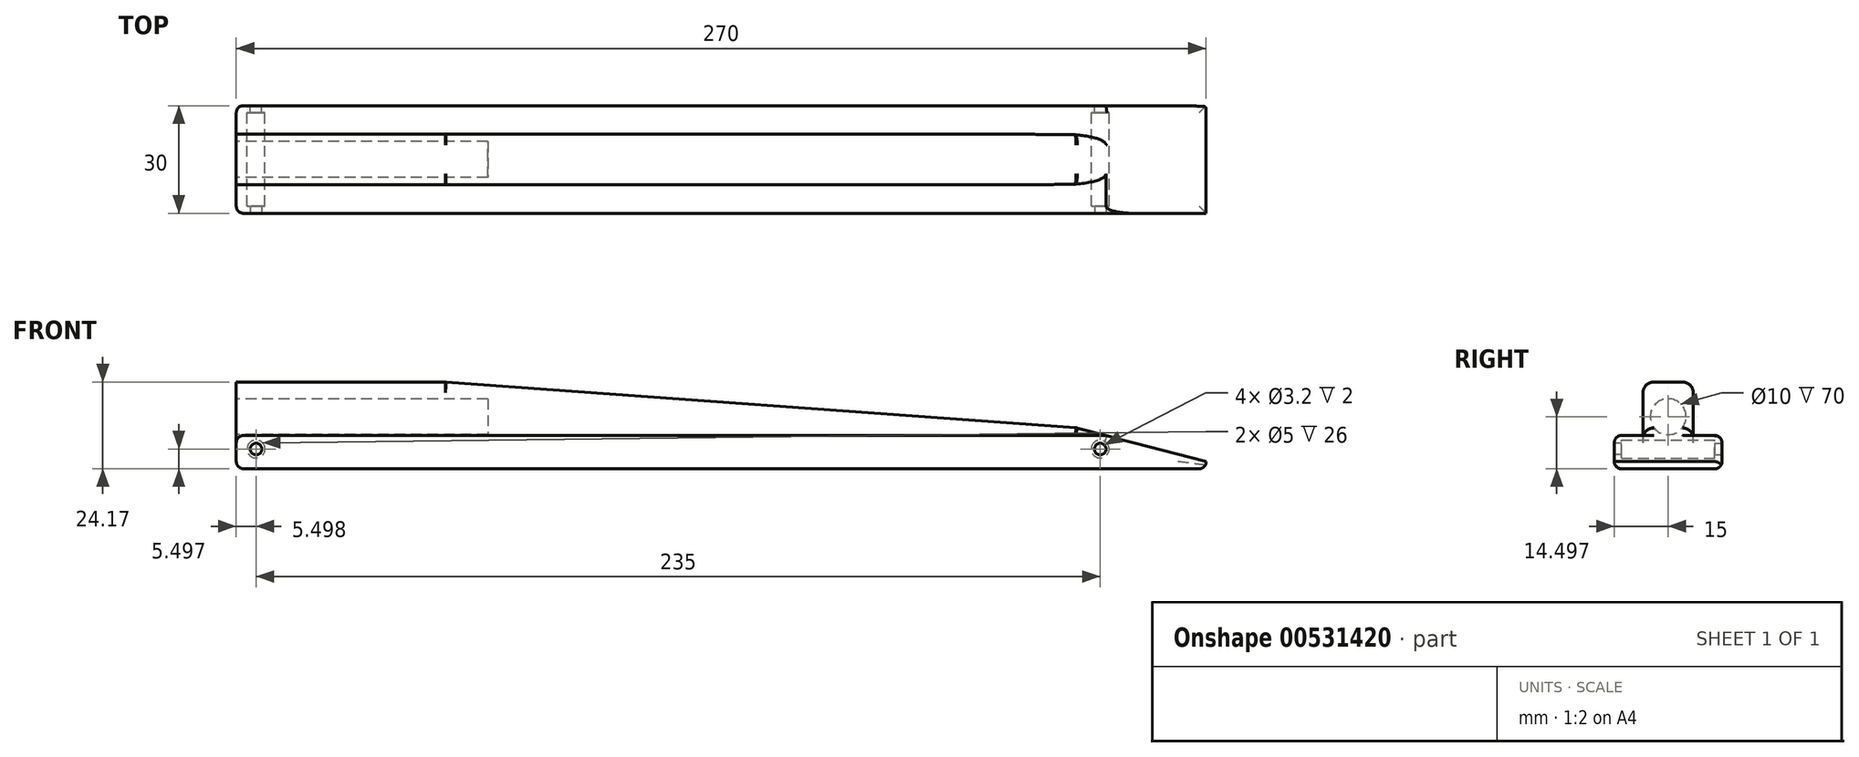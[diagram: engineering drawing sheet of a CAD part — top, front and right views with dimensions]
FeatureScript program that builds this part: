
annotation { "Feature Type Name" : "Feature", "Feature Type Description" : "" }
export const myFeature = defineFeature(function(context is Context, id is Id, definition is map)
    precondition{}
    {
        {
            var Q0;
            Q0=qCreatedBy(makeId("Front.planeOp"),FACE);
            var sketch = newSketch(context, id + "F0", { "sketchPlane" : qUnion([Q0])});
            skLineSegment(sketch, "E0.bottom", {"start": v(-113.44, 3.04) * mm, "end": v(136.56, 3.04) * mm});
            skLineSegment(sketch, "E0.top", {"start": v(-113.44, -36.96) * mm, "end": v(136.56, -36.96) * mm});
            skLineSegment(sketch, "E0.left", {"start": v(-113.44, 3.04) * mm, "end": v(-113.44, -36.96) * mm});
            skLineSegment(sketch, "E0.right", {"start": v(136.56, 3.04) * mm, "end": v(136.56, -36.96) * mm});
            skCircle(sketch, "E1", {"center": v(-107.94, -31.46) * mm, "radius": 2.5 * mm});
            skCircle(sketch, "E2", {"center": v(-107.94, -31.46) * mm, "radius": 1.6 * mm});
            skCircle(sketch, "E3", {"center": v(127.06, -31.46) * mm, "radius": 2.5 * mm});
            skCircle(sketch, "E4", {"center": v(127.06, -31.46) * mm, "radius": 1.6 * mm});
            skSolve(sketch);
        }
        {
            var Q0;
            Q0=makeQuery(id+"F0.imprint","IMPRINT",FACE,{"disambiguationData":[TD([[makeQuery(id+"F0.imprint","IMPRINT",EDGE,{"derivedFrom":sQuery(id+"F0.wireOp",EDGE,"E0.bottom")}),-1.0]])]});
            extrude(context, id + "F1", {"entities" : qUnion([Q0]), "depth" : 15 * mm, "offsetDistance" : 25 * mm, "hasSecondDirection" : true, "secondDirectionOppositeDirection" : true, "secondDirectionDepth" : 15 * mm});
        }
        {
            var Q0;
            Q0=makeQuery(id+"F1.opExtrude","CAP_FACE",FACE,{"disambiguationData":[OSD([sQuery(id+"F0.wireOp",EDGE,"E0.bottom"),sQuery(id+"F0.wireOp",EDGE,"E0.top"),sQuery(id+"F0.wireOp",EDGE,"E0.left"),sQuery(id+"F0.wireOp",EDGE,"E0.right"),sQuery(id+"F0.wireOp",EDGE,"E1"),sQuery(id+"F0.wireOp",EDGE,"E3")])],"isStart":false});
            var sketch = newSketch(context, id + "F2", { "sketchPlane" : qUnion([Q0])});
            skLineSegment(sketch, "E5.bottom", {"start": v(-113.44, 3.04) * mm, "end": v(136.56, 3.04) * mm});
            skLineSegment(sketch, "E5.top", {"start": v(-113.44, -36.96) * mm, "end": v(136.56, -36.96) * mm});
            skLineSegment(sketch, "E5.left", {"start": v(-113.44, 3.04) * mm, "end": v(-113.44, -36.96) * mm});
            skLineSegment(sketch, "E5.right", {"start": v(136.56, 3.04) * mm, "end": v(136.56, -36.96) * mm});
            skCircle(sketch, "E6", {"center": v(-107.94, -31.46) * mm, "radius": 2.5 * mm});
            skCircle(sketch, "E7", {"center": v(-107.94, -31.46) * mm, "radius": 1.6 * mm});
            skCircle(sketch, "E8", {"center": v(127.06, -31.46) * mm, "radius": 2.5 * mm});
            skCircle(sketch, "E9", {"center": v(127.06, -31.46) * mm, "radius": 1.6 * mm});
            skSolve(sketch);
        }
        {
            var Q0;
            Q0=makeQuery(id+"F2.imprint","IMPRINT",FACE,{"disambiguationData":[TD([[makeQuery(id+"F2.imprint","IMPRINT",EDGE,{"derivedFrom":sQuery(id+"F2.wireOp",EDGE,"E6")}),1.0]])]});
            var Q1;
            Q1=makeQuery(id+"F2.imprint","IMPRINT",FACE,{"disambiguationData":[TD([[makeQuery(id+"F2.imprint","IMPRINT",EDGE,{"derivedFrom":sQuery(id+"F2.wireOp",EDGE,"E8")}),1.0]])]});
            extrude(context, id + "F3", {"entities" : qUnion([Q0, Q1]), "operationType" : NewBodyOperationType.ADD, "oppositeDirection" : true, "depth" : 2 * mm, "offsetDistance" : 25 * mm});
        }
        {
            var Q0;
            Q0=makeQuery(id+"F1.opExtrude","CAP_FACE",FACE,{"disambiguationData":[OSD([sQuery(id+"F0.wireOp",EDGE,"E0.bottom"),sQuery(id+"F0.wireOp",EDGE,"E0.top"),sQuery(id+"F0.wireOp",EDGE,"E0.left"),sQuery(id+"F0.wireOp",EDGE,"E0.right"),sQuery(id+"F0.wireOp",EDGE,"E1"),sQuery(id+"F0.wireOp",EDGE,"E3")])],"isStart":true});
            var sketch = newSketch(context, id + "F4", { "sketchPlane" : qUnion([Q0])});
            skLineSegment(sketch, "E10.bottom", {"start": v(-136.56, 3.04) * mm, "end": v(113.44, 3.04) * mm});
            skLineSegment(sketch, "E10.top", {"start": v(-136.56, -36.96) * mm, "end": v(113.44, -36.96) * mm});
            skLineSegment(sketch, "E10.left", {"start": v(-136.56, 3.04) * mm, "end": v(-136.56, -36.96) * mm});
            skLineSegment(sketch, "E10.right", {"start": v(113.44, 3.04) * mm, "end": v(113.44, -36.96) * mm});
            skCircle(sketch, "E11", {"center": v(-127.06, -31.46) * mm, "radius": 2.5 * mm});
            skCircle(sketch, "E12", {"center": v(-127.06, -31.46) * mm, "radius": 1.6 * mm});
            skCircle(sketch, "E13", {"center": v(107.94, -31.46) * mm, "radius": 2.5 * mm});
            skCircle(sketch, "E14", {"center": v(107.94, -31.46) * mm, "radius": 1.6 * mm});
            skSolve(sketch);
        }
        {
            var Q0;
            Q0=makeQuery(id+"F4.imprint","IMPRINT",FACE,{"disambiguationData":[TD([[makeQuery(id+"F4.imprint","IMPRINT",EDGE,{"derivedFrom":sQuery(id+"F4.wireOp",EDGE,"E13")}),-1.0]])]});
            var Q1;
            Q1=makeQuery(id+"F4.imprint","IMPRINT",FACE,{"disambiguationData":[TD([[makeQuery(id+"F4.imprint","IMPRINT",EDGE,{"derivedFrom":sQuery(id+"F4.wireOp",EDGE,"E11")}),-1.0]])]});
            extrude(context, id + "F5", {"entities" : qUnion([Q0, Q1]), "operationType" : NewBodyOperationType.ADD, "oppositeDirection" : true, "depth" : 2 * mm, "offsetDistance" : 25 * mm});
        }
        {
            var Q0;
            Q0=makeQuery(id+"F1.opExtrude","SWEPT_FACE",FACE,{"disambiguationData":[OSD([sQuery(id+"F0.wireOp",EDGE,"E0.left")])]});
            var sketch = newSketch(context, id + "F6", { "sketchPlane" : qUnion([Q0])});
            skCircle(sketch, "E15", {"center": v(0, -22.46) * mm, "radius": 5 * mm});
            skPoint(sketch, "E15.centerSnap0", {"position": v(0, -36.96) * mm});
            skSolve(sketch);
        }
        {
            var Q0;
            Q0=makeQuery(id+"F6.imprint","IMPRINT",FACE,{"disambiguationData":[TD([[makeQuery(id+"F6.imprint","IMPRINT",EDGE,{"derivedFrom":sQuery(id+"F6.wireOp",EDGE,"E15")}),1.0]])]});
            extrude(context, id + "F7", {"entities" : qUnion([Q0]), "operationType" : NewBodyOperationType.REMOVE, "oppositeDirection" : true, "depth" : 70 * mm, "offsetDistance" : 25 * mm});
        }
        {
            var Q0;
            Q0=makeQuery(id+"F1.opExtrude","SWEPT_FACE",FACE,{"disambiguationData":[OSD([sQuery(id+"F0.wireOp",EDGE,"E0.right")])]});
            extrude(context, id + "F8", {"entities" : qUnion([Q0]), "operationType" : NewBodyOperationType.ADD, "depth" : 20 * mm, "offsetDistance" : 25 * mm});
        }
        {
            var Q0;
            {var subQ0=sQuery(id+"F0.wireOp",EDGE,"E0.right");Q0=makeQuery(id+"F8.boolean.opBoolean","MERGE",FACE,{"derivedFrom":[makeQuery(id+"F3.boolean.opBoolean","MERGE",FACE,{"derivedFrom":[makeQuery(id+"F1.opExtrude","CAP_FACE",FACE,{"disambiguationData":[OSD([sQuery(id+"F0.wireOp",EDGE,"E0.bottom"),sQuery(id+"F0.wireOp",EDGE,"E0.top"),sQuery(id+"F0.wireOp",EDGE,"E0.left"),subQ0,sQuery(id+"F0.wireOp",EDGE,"E1"),sQuery(id+"F0.wireOp",EDGE,"E3")])],"isStart":false}),makeQuery(id+"F3.opExtrude","CAP_FACE",FACE,{"disambiguationData":[OSD([sQuery(id+"F2.wireOp",EDGE,"E6"),sQuery(id+"F2.wireOp",EDGE,"E7")])],"isStart":true}),makeQuery(id+"F3.opExtrude","CAP_FACE",FACE,{"disambiguationData":[OSD([sQuery(id+"F2.wireOp",EDGE,"E8"),sQuery(id+"F2.wireOp",EDGE,"E9")])],"isStart":true})]}),makeQuery(id+"F8.opExtrude","SWEPT_FACE",FACE,{"disambiguationData":[OSD([subQ0]),TDD([makeQuery(id+"F1.opExtrude","CAP_EDGE",EDGE,{"disambiguationData":[OSD([subQ0])],"isStart":false})])]})]});}
            var sketch = newSketch(context, id + "F9", { "sketchPlane" : qUnion([Q0])});
            skLineSegment(sketch, "E16", {"start": v(156.56, -34.96) * mm, "end": v(120.52, -25.57) * mm});
            skLineSegment(sketch, "E17", {"start": v(120.52, -25.57) * mm, "end": v(-55.11, -12.8) * mm});
            skLineSegment(sketch, "E18", {"start": v(-55.11, -12.8) * mm, "end": v(-113.44, -12.8) * mm});
            skSolve(sketch);
        }
        {
            var Q0;
            {var subQ4=sQuery(id+"F9.wireOp",EDGE,"E16");Q0=makeQuery(id+"F9.imprint","IMPRINT",FACE,{"disambiguationData":[TD([[makeQuery(id+"F9.imprint","IMPRINT",EDGE,{"derivedFrom":subQ4}),-1.0]])]});}
            extrude(context, id + "F10", {"entities" : qUnion([Q0]), "operationType" : NewBodyOperationType.REMOVE, "endBound" : BoundingType.THROUGH_ALL, "oppositeDirection" : true, "depth" : 25 * mm, "offsetDistance" : 25 * mm});
        }
        {
            var Q0;
            Q0=makeQuery(id+"F10.boolean.opBoolean","COPY",EDGE,{"derivedFrom":makeQuery(id+"F10.opExtrude","SWEPT_EDGE",EDGE,{"disambiguationData":[OSD([sQuery(id+"F0.wireOp",EDGE,"E0.right"),sQuery(id+"F9.wireOp",EDGE,"E16")])]})});
            var Q1;
            Q1=makeQuery(id+"F10.boolean.opBoolean","COPY",EDGE,{"derivedFrom":makeQuery(id+"F10.opExtrude","SWEPT_EDGE",EDGE,{"disambiguationData":[OSD([sQuery(id+"F9.wireOp",EDGE,"E16"),sQuery(id+"F9.wireOp",EDGE,"E17")])]})});
            var Q2;
            Q2=makeQuery(id+"F10.boolean.opBoolean","COPY",EDGE,{"derivedFrom":makeQuery(id+"F10.opExtrude","CAP_EDGE",EDGE,{"disambiguationData":[OSD([sQuery(id+"F9.wireOp",EDGE,"E18")])],"isStart":true})});
            var Q3;
            Q3=makeQuery(id+"F10.boolean.opBoolean","COPY",EDGE,{"derivedFrom":makeQuery(id+"F10.opExtrude","CAP_EDGE",EDGE,{"disambiguationData":[OSD([sQuery(id+"F9.wireOp",EDGE,"E17")])],"isStart":true})});
            var Q4;
            Q4=makeQuery(id+"F10.boolean.opBoolean","COPY",EDGE,{"derivedFrom":makeQuery(id+"F10.opExtrude","CAP_EDGE",EDGE,{"disambiguationData":[OSD([sQuery(id+"F9.wireOp",EDGE,"E16")])],"isStart":true})});
            var Q5;
            {var subQ0=sQuery(id+"F0.wireOp",EDGE,"E0.right");Q5=makeQuery(id+"F10.boolean.opBoolean","INTERSECT",EDGE,{"derivedFrom":[makeQuery(id+"F8.boolean.opBoolean","MERGE",FACE,{"derivedFrom":[makeQuery(id+"F5.boolean.opBoolean","MERGE",FACE,{"derivedFrom":[makeQuery(id+"F1.opExtrude","CAP_FACE",FACE,{"disambiguationData":[OSD([sQuery(id+"F0.wireOp",EDGE,"E0.bottom"),sQuery(id+"F0.wireOp",EDGE,"E0.top"),sQuery(id+"F0.wireOp",EDGE,"E0.left"),subQ0,sQuery(id+"F0.wireOp",EDGE,"E1"),sQuery(id+"F0.wireOp",EDGE,"E3")])],"isStart":true}),makeQuery(id+"F5.opExtrude","CAP_FACE",FACE,{"disambiguationData":[OSD([sQuery(id+"F4.wireOp",EDGE,"E11"),sQuery(id+"F4.wireOp",EDGE,"E12")])],"isStart":true}),makeQuery(id+"F5.opExtrude","CAP_FACE",FACE,{"disambiguationData":[OSD([sQuery(id+"F4.wireOp",EDGE,"E13"),sQuery(id+"F4.wireOp",EDGE,"E14")])],"isStart":true})]}),makeQuery(id+"F8.opExtrude","SWEPT_FACE",FACE,{"disambiguationData":[OSD([subQ0]),TDD([makeQuery(id+"F1.opExtrude","CAP_EDGE",EDGE,{"disambiguationData":[OSD([subQ0])],"isStart":true})])]})]}),makeQuery(id+"F10.opExtrude","SWEPT_FACE",FACE,{"disambiguationData":[OSD([sQuery(id+"F9.wireOp",EDGE,"E16")])]})]});}
            var Q6;
            {var subQ0=sQuery(id+"F0.wireOp",EDGE,"E0.right");Q6=makeQuery(id+"F10.boolean.opBoolean","INTERSECT",EDGE,{"derivedFrom":[makeQuery(id+"F8.boolean.opBoolean","MERGE",FACE,{"derivedFrom":[makeQuery(id+"F5.boolean.opBoolean","MERGE",FACE,{"derivedFrom":[makeQuery(id+"F1.opExtrude","CAP_FACE",FACE,{"disambiguationData":[OSD([sQuery(id+"F0.wireOp",EDGE,"E0.bottom"),sQuery(id+"F0.wireOp",EDGE,"E0.top"),sQuery(id+"F0.wireOp",EDGE,"E0.left"),subQ0,sQuery(id+"F0.wireOp",EDGE,"E1"),sQuery(id+"F0.wireOp",EDGE,"E3")])],"isStart":true}),makeQuery(id+"F5.opExtrude","CAP_FACE",FACE,{"disambiguationData":[OSD([sQuery(id+"F4.wireOp",EDGE,"E11"),sQuery(id+"F4.wireOp",EDGE,"E12")])],"isStart":true}),makeQuery(id+"F5.opExtrude","CAP_FACE",FACE,{"disambiguationData":[OSD([sQuery(id+"F4.wireOp",EDGE,"E13"),sQuery(id+"F4.wireOp",EDGE,"E14")])],"isStart":true})]}),makeQuery(id+"F8.opExtrude","SWEPT_FACE",FACE,{"disambiguationData":[OSD([subQ0]),TDD([makeQuery(id+"F1.opExtrude","CAP_EDGE",EDGE,{"disambiguationData":[OSD([subQ0])],"isStart":true})])]})]}),makeQuery(id+"F10.opExtrude","SWEPT_FACE",FACE,{"disambiguationData":[OSD([sQuery(id+"F9.wireOp",EDGE,"E17")])]})]});}
            var Q7;
            Q7=makeQuery(id+"F10.boolean.opBoolean","COPY",EDGE,{"derivedFrom":makeQuery(id+"F10.opExtrude","SWEPT_EDGE",EDGE,{"disambiguationData":[OSD([sQuery(id+"F0.wireOp",EDGE,"E0.left"),sQuery(id+"F9.wireOp",EDGE,"E18")])]})});
            var Q8;
            Q8=makeQuery(id+"F1.opExtrude","CAP_EDGE",EDGE,{"disambiguationData":[OSD([sQuery(id+"F0.wireOp",EDGE,"E0.left")])],"isStart":true});
            var Q9;
            Q9=makeQuery(id+"F1.opExtrude","SWEPT_EDGE",EDGE,{"disambiguationData":[OSD([sQuery(id+"F0.wireOp",EDGE,"E0.top"),sQuery(id+"F0.wireOp",EDGE,"E0.left")])]});
            var Q10;
            Q10=makeQuery(id+"F1.opExtrude","CAP_EDGE",EDGE,{"disambiguationData":[OSD([sQuery(id+"F0.wireOp",EDGE,"E0.left")])],"isStart":false});
            var Q11;
            {var subQ0=sQuery(id+"F0.wireOp",EDGE,"E0.right");var subQ1=sQuery(id+"F0.wireOp",EDGE,"E0.top");Q11=makeQuery(id+"F8.boolean.opBoolean","MERGE",EDGE,{"derivedFrom":[makeQuery(id+"F1.opExtrude","CAP_EDGE",EDGE,{"disambiguationData":[OSD([subQ1])],"isStart":true}),makeQuery(id+"F8.opExtrude","SWEPT_EDGE",EDGE,{"disambiguationData":[OSD([subQ1,subQ0]),TDD([makeQuery(id+"F1.opExtrude","CAP_VERTEX",VERTEX,{"disambiguationData":[OSD([subQ1,subQ0])],"isStart":true})])]})]});}
            var Q12;
            {var subQ0=sQuery(id+"F0.wireOp",EDGE,"E0.right");var subQ1=sQuery(id+"F0.wireOp",EDGE,"E0.top");Q12=makeQuery(id+"F8.boolean.opBoolean","MERGE",EDGE,{"derivedFrom":[makeQuery(id+"F1.opExtrude","CAP_EDGE",EDGE,{"disambiguationData":[OSD([subQ1])],"isStart":false}),makeQuery(id+"F8.opExtrude","SWEPT_EDGE",EDGE,{"disambiguationData":[OSD([subQ1,subQ0]),TDD([makeQuery(id+"F1.opExtrude","CAP_VERTEX",VERTEX,{"disambiguationData":[OSD([subQ1,subQ0])],"isStart":false})])]})]});}
            var Q13;
            Q13=makeQuery(id+"F8.opExtrude","CAP_EDGE",EDGE,{"disambiguationData":[OSD([sQuery(id+"F0.wireOp",EDGE,"E0.top"),sQuery(id+"F0.wireOp",EDGE,"E0.right")])],"isStart":false});
            var Q14;
            {var subQ0=sQuery(id+"F0.wireOp",EDGE,"E0.right");Q14=makeQuery(id+"F10.boolean.opBoolean","INTERSECT",EDGE,{"derivedFrom":[makeQuery(id+"F8.boolean.opBoolean","MERGE",FACE,{"derivedFrom":[makeQuery(id+"F5.boolean.opBoolean","MERGE",FACE,{"derivedFrom":[makeQuery(id+"F1.opExtrude","CAP_FACE",FACE,{"disambiguationData":[OSD([sQuery(id+"F0.wireOp",EDGE,"E0.bottom"),sQuery(id+"F0.wireOp",EDGE,"E0.top"),sQuery(id+"F0.wireOp",EDGE,"E0.left"),subQ0,sQuery(id+"F0.wireOp",EDGE,"E1"),sQuery(id+"F0.wireOp",EDGE,"E3")])],"isStart":true}),makeQuery(id+"F5.opExtrude","CAP_FACE",FACE,{"disambiguationData":[OSD([sQuery(id+"F4.wireOp",EDGE,"E11"),sQuery(id+"F4.wireOp",EDGE,"E12")])],"isStart":true}),makeQuery(id+"F5.opExtrude","CAP_FACE",FACE,{"disambiguationData":[OSD([sQuery(id+"F4.wireOp",EDGE,"E13"),sQuery(id+"F4.wireOp",EDGE,"E14")])],"isStart":true})]}),makeQuery(id+"F8.opExtrude","SWEPT_FACE",FACE,{"disambiguationData":[OSD([subQ0]),TDD([makeQuery(id+"F1.opExtrude","CAP_EDGE",EDGE,{"disambiguationData":[OSD([subQ0])],"isStart":true})])]})]}),makeQuery(id+"F10.opExtrude","SWEPT_FACE",FACE,{"disambiguationData":[OSD([sQuery(id+"F9.wireOp",EDGE,"E18")])]})]});}
            var Q15;
            Q15=makeQuery(id+"F10.boolean.opBoolean","COPY",EDGE,{"derivedFrom":makeQuery(id+"F10.opExtrude","SWEPT_EDGE",EDGE,{"disambiguationData":[OSD([sQuery(id+"F9.wireOp",EDGE,"E17"),sQuery(id+"F9.wireOp",EDGE,"E18")])]})});
            fillet(context, id + "F11", {"entities" : qUnion([Q0, Q1, Q2, Q3, Q4, Q5, Q6, Q7, Q8, Q9, Q10, Q11, Q12, Q13, Q14, Q15]), "radius" : 2 * mm, "tangentPropagation" : true, "allowEdgeOverflow" : false});
        }
        {
            var Q0;
            Q0=makeQuery(id+"F1.opExtrude","SWEPT_FACE",FACE,{"disambiguationData":[OSD([sQuery(id+"F0.wireOp",EDGE,"E0.left")])]});
            var sketch = newSketch(context, id + "F12", { "sketchPlane" : qUnion([Q0])});
            skLineSegment(sketch, "E19", {"start": v(-7, -14.8) * mm, "end": v(-7, -27.68) * mm});
            skLineSegment(sketch, "E20", {"start": v(-7, -27.68) * mm, "end": v(-31.2, -27.68) * mm});
            skLineSegment(sketch, "E21", {"start": v(-31.2, -27.68) * mm, "end": v(-31.2, -5.98) * mm});
            skLineSegment(sketch, "E22", {"start": v(-31.2, -5.98) * mm, "end": v(-7, -5.98) * mm});
            skLineSegment(sketch, "E23", {"start": v(-7, -5.98) * mm, "end": v(-7, -14.8) * mm});
            skLineSegment(sketch, "E24", {"start": v(7, -27.68) * mm, "end": v(7, -2) * mm});
            skLineSegment(sketch, "E25", {"start": v(7, -2) * mm, "end": v(55.28, -2) * mm});
            skLineSegment(sketch, "E26", {"start": v(55.28, -2) * mm, "end": v(55.28, -27.68) * mm});
            skLineSegment(sketch, "E27", {"start": v(55.28, -27.68) * mm, "end": v(7, -27.68) * mm});
            skSolve(sketch);
        }
        {
            var Q0;
            {var subQ0=sQuery(id+"F12.wireOp",EDGE,"E19");Q0=makeQuery(id+"F12.imprint","IMPRINT",FACE,{"disambiguationData":[TD([[makeQuery(id+"F12.imprint","IMPRINT",EDGE,{"derivedFrom":subQ0}),-1.0]])]});}
            var Q1;
            {var subQ0=sQuery(id+"F12.wireOp",EDGE,"E27");var subQ1=sQuery(id+"F12.wireOp",EDGE,"E24");var subQ2=makeQuery(id+"F12.imprint","INTERSECT",VERTEX,{"derivedFrom":[subQ1,subQ0]});Q1=makeQuery(id+"F12.imprint","IMPRINT",FACE,{"disambiguationData":[TD([[makeQuery(id+"F12.imprint","IMPRINT",EDGE,{"disambiguationData":[TD([[subQ2,1.0]])],"derivedFrom":subQ0}),-1.0]])]});}
            var Q2;
            {var subQ1=sQuery(id+"F12.wireOp",EDGE,"E21");Q2=makeQuery(id+"F12.imprint","IMPRINT",FACE,{"disambiguationData":[TD([[makeQuery(id+"F12.imprint","IMPRINT",EDGE,{"derivedFrom":subQ1}),-1.0]])]});}
            var Q3;
            {var subQ8=sQuery(id+"F12.wireOp",EDGE,"E25");Q3=makeQuery(id+"F12.imprint","IMPRINT",FACE,{"disambiguationData":[TD([[makeQuery(id+"F12.imprint","IMPRINT",EDGE,{"derivedFrom":subQ8}),-1.0]])]});}
            extrude(context, id + "F13", {"entities" : qUnion([Q0, Q1, Q2, Q3]), "operationType" : NewBodyOperationType.REMOVE, "endBound" : BoundingType.THROUGH_ALL, "oppositeDirection" : true, "depth" : 25 * mm, "offsetDistance" : 25 * mm});
        }
        {
            var Q0;
            Q0=makeQuery(id+"F13.boolean.opBoolean","INTERSECT",EDGE,{"derivedFrom":[makeQuery(id+"F10.boolean.opBoolean","COPY",FACE,{"derivedFrom":makeQuery(id+"F10.opExtrude","SWEPT_FACE",FACE,{"disambiguationData":[OSD([sQuery(id+"F9.wireOp",EDGE,"E16")])]})}),makeQuery(id+"F13.opExtrude","SWEPT_FACE",FACE,{"disambiguationData":[OSD([sQuery(id+"F12.wireOp",EDGE,"E24")])]})]});
            var Q1;
            Q1=makeQuery(id+"F13.boolean.opBoolean","INTERSECT",EDGE,{"derivedFrom":[makeQuery(id+"F10.boolean.opBoolean","COPY",FACE,{"derivedFrom":makeQuery(id+"F10.opExtrude","SWEPT_FACE",FACE,{"disambiguationData":[OSD([sQuery(id+"F9.wireOp",EDGE,"E16")])]})}),makeQuery(id+"F13.opExtrude","SWEPT_FACE",FACE,{"disambiguationData":[OSD([sQuery(id+"F12.wireOp",EDGE,"E19"),sQuery(id+"F12.wireOp",EDGE,"E23")])]})]});
            fillet(context, id + "F14", {"entities" : qUnion([Q0, Q1]), "radius" : 3 * mm, "tangentPropagation" : true, "allowEdgeOverflow" : false});
        }
        {
            var Q0;
            {var subQ0=sQuery(id+"F0.wireOp",EDGE,"E0.right");Q0=makeQuery(id+"F13.boolean.opBoolean","INTERSECT",EDGE,{"derivedFrom":[makeQuery(id+"F8.boolean.opBoolean","MERGE",FACE,{"derivedFrom":[makeQuery(id+"F3.boolean.opBoolean","MERGE",FACE,{"derivedFrom":[makeQuery(id+"F1.opExtrude","CAP_FACE",FACE,{"disambiguationData":[OSD([sQuery(id+"F0.wireOp",EDGE,"E0.bottom"),sQuery(id+"F0.wireOp",EDGE,"E0.top"),sQuery(id+"F0.wireOp",EDGE,"E0.left"),subQ0,sQuery(id+"F0.wireOp",EDGE,"E1"),sQuery(id+"F0.wireOp",EDGE,"E3")])],"isStart":false}),makeQuery(id+"F3.opExtrude","CAP_FACE",FACE,{"disambiguationData":[OSD([sQuery(id+"F2.wireOp",EDGE,"E6"),sQuery(id+"F2.wireOp",EDGE,"E7")])],"isStart":true}),makeQuery(id+"F3.opExtrude","CAP_FACE",FACE,{"disambiguationData":[OSD([sQuery(id+"F2.wireOp",EDGE,"E8"),sQuery(id+"F2.wireOp",EDGE,"E9")])],"isStart":true})]}),makeQuery(id+"F8.opExtrude","SWEPT_FACE",FACE,{"disambiguationData":[OSD([subQ0]),TDD([makeQuery(id+"F1.opExtrude","CAP_EDGE",EDGE,{"disambiguationData":[OSD([subQ0])],"isStart":false})])]})]}),makeQuery(id+"F13.opExtrude","SWEPT_FACE",FACE,{"disambiguationData":[OSD([sQuery(id+"F12.wireOp",EDGE,"E27")])]})]});}
            var Q1;
            {var subQ0=sQuery(id+"F0.wireOp",EDGE,"E0.right");Q1=makeQuery(id+"F13.boolean.opBoolean","INTERSECT",EDGE,{"derivedFrom":[makeQuery(id+"F8.boolean.opBoolean","MERGE",FACE,{"derivedFrom":[makeQuery(id+"F5.boolean.opBoolean","MERGE",FACE,{"derivedFrom":[makeQuery(id+"F1.opExtrude","CAP_FACE",FACE,{"disambiguationData":[OSD([sQuery(id+"F0.wireOp",EDGE,"E0.bottom"),sQuery(id+"F0.wireOp",EDGE,"E0.top"),sQuery(id+"F0.wireOp",EDGE,"E0.left"),subQ0,sQuery(id+"F0.wireOp",EDGE,"E1"),sQuery(id+"F0.wireOp",EDGE,"E3")])],"isStart":true}),makeQuery(id+"F5.opExtrude","CAP_FACE",FACE,{"disambiguationData":[OSD([sQuery(id+"F4.wireOp",EDGE,"E11"),sQuery(id+"F4.wireOp",EDGE,"E12")])],"isStart":true}),makeQuery(id+"F5.opExtrude","CAP_FACE",FACE,{"disambiguationData":[OSD([sQuery(id+"F4.wireOp",EDGE,"E13"),sQuery(id+"F4.wireOp",EDGE,"E14")])],"isStart":true})]}),makeQuery(id+"F8.opExtrude","SWEPT_FACE",FACE,{"disambiguationData":[OSD([subQ0]),TDD([makeQuery(id+"F1.opExtrude","CAP_EDGE",EDGE,{"disambiguationData":[OSD([subQ0])],"isStart":true})])]})]}),makeQuery(id+"F13.opExtrude","SWEPT_FACE",FACE,{"disambiguationData":[OSD([sQuery(id+"F12.wireOp",EDGE,"E20")])]})]});}
            fillet(context, id + "F15", {"entities" : qUnion([Q0, Q1]), "radius" : 2 * mm, "tangentPropagation" : true, "allowEdgeOverflow" : false});
        }
    });
